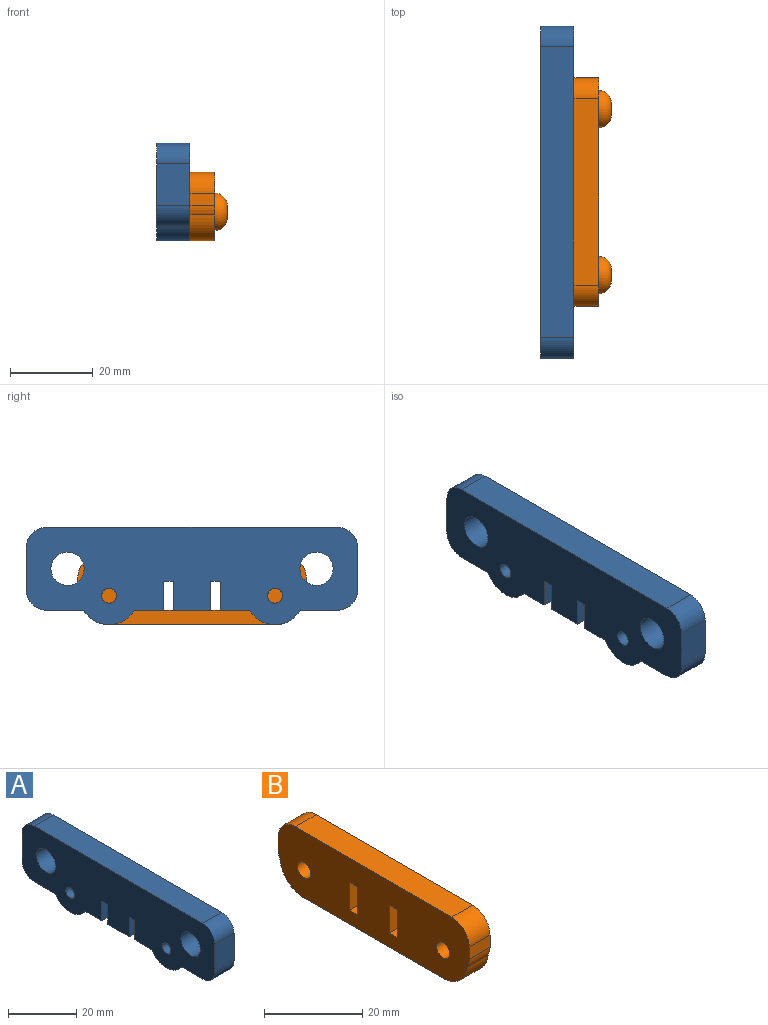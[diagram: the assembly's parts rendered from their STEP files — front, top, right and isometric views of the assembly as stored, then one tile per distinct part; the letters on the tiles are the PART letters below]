
ASSEMBLY  parts=2 mates=1
PART A: 40 faces, bbox 8x80x23.5 mm
  f0: cylinder r=1.8mm len=5mm, axis (-1,0,0), area 56.5mm2, adj f25,f39
  f1: cylinder r=1.8mm len=5mm, axis (-1,0,0), area 56.5mm2, adj f25,f32
  f2: plane 80x23.5mm, normal (1,0,0), area 1450.3mm2, adj f3,f4,f5,f6,f7,f8,f9,f10
  f3: plane 8x2.4mm, normal (0,0,-1), area 19.2mm2, adj f2,f4,f24,f25
  f4: plane 8x7mm, normal (0,-1,0), area 56mm2, adj f2,f3,f5,f25
  f5: plane 8x7.04mm, normal (0,0,-1), area 56.3mm2, adj f2,f4,f6,f25
  f6: cylinder r=7mm len=12.12mm, axis (-1,0,0), area 117.3mm2, adj f2,f5,f7,f25
  f7: plane 8.94x8mm, normal (0,0,-1), area 71.5mm2, adj f2,f6,f8,f25
  f8: cylinder r=5mm len=8mm, axis (-1,0,0), area 62.8mm2, adj f2,f7,f9,f25
  f9: plane 10x8mm, normal (0,1,0), area 80mm2, adj f2,f8,f10,f25
  f10: cylinder r=5mm len=8mm, axis (-1,0,0), area 62.8mm2, adj f2,f9,f11,f25
  f11: plane 70x8mm, normal (0,0,1), area 560mm2, adj f2,f10,f12,f25
  f12: cylinder r=5mm len=8mm, axis (-1,0,0), area 62.8mm2, adj f2,f11,f13,f25
  f13: plane 10x8mm, normal (0,-1,0), area 80mm2, adj f2,f12,f14,f25
  f14: cylinder r=5mm len=8mm, axis (-1,0,0), area 62.8mm2, adj f2,f13,f15,f25
  f15: plane 8.94x8mm, normal (0,0,-1), area 71.5mm2, adj f2,f14,f16,f25
  f16: cylinder r=7mm len=12.12mm, axis (-1,0,0), area 117.3mm2, adj f2,f15,f17,f25
  f17: plane 8x7.04mm, normal (0,0,-1), area 56.3mm2, adj f2,f16,f18,f25
  f18: plane 8x7mm, normal (0,1,0), area 56mm2, adj f2,f17,f19,f25
  f19: plane 8x2.4mm, normal (0,0,-1), area 19.2mm2, adj f2,f18,f20,f25
  f20: plane 8x7mm, normal (0,-1,0), area 56mm2, adj f2,f19,f21,f25
  f21: plane 9x8mm, normal (0,0,-1), area 72mm2, adj f2,f20,f24,f25
  f22: cylinder r=4mm len=8mm, axis (-1,0,0), area 201.1mm2, adj f2,f25
  f23: cylinder r=4mm len=8mm, axis (-1,0,0), area 201.1mm2, adj f2,f25
  f24: plane 8x7mm, normal (0,1,0), area 56mm2, adj f2,f3,f21,f25
  f25: plane 80x23.5mm, normal (-1,0,0), area 1484.2mm2, adj f0,f1,f3,f4,f5,f6,f7,f8
  f26: plane 3x2.8mm, normal (0,0.87,-0.5), area 9.7mm2, adj f2,f27,f31,f32
  f27: plane 3x2.8mm, normal (0,0.87,0.5), area 9.7mm2, adj f2,f26,f28,f32
  f28: plane 3.23x3mm, normal (0,0,1), area 9.7mm2, adj f2,f27,f29,f32
  f29: plane 3x2.8mm, normal (0,-0.87,0.5), area 9.7mm2, adj f2,f28,f30,f32
  f30: plane 3x2.8mm, normal (0,-0.87,-0.5), area 9.7mm2, adj f2,f29,f31,f32
  f31: plane 3.23x3mm, normal (0,0,-1), area 9.7mm2, adj f2,f26,f30,f32
  f32: plane 6.47x5.6mm, normal (1,0,0), area 17mm2, adj f1,f26,f27,f28,f29,f30,f31
  f33: plane 3x2.8mm, normal (0,0.87,-0.5), area 9.7mm2, adj f2,f34,f38,f39
  f34: plane 3x2.8mm, normal (0,0.87,0.5), area 9.7mm2, adj f2,f33,f35,f39
  f35: plane 3.23x3mm, normal (0,0,1), area 9.7mm2, adj f2,f34,f36,f39
  f36: plane 3x2.8mm, normal (0,-0.87,0.5), area 9.7mm2, adj f2,f35,f37,f39
  f37: plane 3x2.8mm, normal (0,-0.87,-0.5), area 9.7mm2, adj f2,f36,f38,f39
  f38: plane 3.23x3mm, normal (0,0,-1), area 9.7mm2, adj f2,f33,f37,f39
  f39: plane 6.47x5.6mm, normal (1,0,0), area 17mm2, adj f0,f33,f34,f35,f36,f37,f38
PART B: 28 faces, bbox 9x55x16.5 mm
  f0: plane 6x2.4mm, normal (0,0,1), area 14.4mm2, adj f1,f16,f20,f21
  f1: plane 7x6mm, normal (0,1,0), area 42mm2, adj f0,f2,f20,f21
  f2: plane 6x2.4mm, normal (0,0,-1), area 14.4mm2, adj f1,f16,f20,f21
  f3: plane 6x2.4mm, normal (0,0,1), area 14.4mm2, adj f4,f17,f20,f21
  f4: plane 7x6mm, normal (0,1,0), area 42mm2, adj f3,f5,f20,f21
  f5: plane 6x2.4mm, normal (0,0,-1), area 14.4mm2, adj f4,f17,f20,f21
  f6: cylinder r=7mm len=6.87mm, axis (-1,0,0), area 60.9mm2, adj f7,f18,f20,f21
  f7: plane 40.09x6mm, normal (0,0,-1), area 240.5mm2, adj f6,f8,f20,f21
  f8: cylinder r=7mm len=6.96mm, axis (-1,0,0), area 61.4mm2, adj f7,f9,f20,f21
  f9: cylinder r=5mm len=6mm, axis (-1,0,0), area 14.1mm2, adj f8,f10,f20,f21
  f10: plane 6x3mm, normal (0,1,0), area 18mm2, adj f9,f11,f20,f21
  f11: cylinder r=5mm len=6mm, axis (-1,0,0), area 47.1mm2, adj f10,f12,f20,f21
  f12: plane 45x6mm, normal (0,0,1), area 270mm2, adj f11,f13,f20,f21
  f13: cylinder r=5mm len=6mm, axis (-1,0,0), area 47.1mm2, adj f12,f14,f20,f21
  f14: plane 6x3mm, normal (0,-1,0), area 18mm2, adj f13,f18,f20,f21
  f15: cylinder r=1.9mm len=6mm, axis (-1,0,0), area 71.6mm2, adj f21,f25
  f16: plane 7x6mm, normal (0,-1,0), area 42mm2, adj f0,f2,f20,f21
  f17: plane 7x6mm, normal (0,-1,0), area 42mm2, adj f3,f5,f20,f21
  f18: cylinder r=5mm len=6mm, axis (-1,0,0), area 14.1mm2, adj f6,f14,f20,f21
  f19: cylinder r=1.9mm len=6mm, axis (-1,0,0), area 71.6mm2, adj f21,f23
  f20: plane 55x16.5mm, normal (1,0,0), area 707.9mm2, adj f0,f1,f2,f3,f4,f5,f6,f7
  f21: plane 55x16.5mm, normal (-1,0,0), area 812.4mm2, adj f0,f1,f2,f3,f4,f5,f6,f7
  f22: plane 3x3mm, normal (1,0,0), area 7.1mm2, adj f26
  f23: plane 3.8x3.8mm, normal (-1,0,0), area 11.3mm2, adj f19
  f24: plane 3x3mm, normal (1,0,0), area 7.1mm2, adj f27
  f25: plane 3.8x3.8mm, normal (-1,0,0), area 11.3mm2, adj f15
  f26: torus R=1.5mm, axis (1,0,0), area 101mm2, adj f20,f22
  f27: torus R=1.5mm, axis (1,0,0), area 101mm2, adj f20,f24
PLACE A t=(-34.78,15.1,-17.42)mm
PLACE B t=(-30.78,15.1,49.27)mm
MATE fastened B.f21 <-> A.f2  axis (-1,0,0) through (-30.78,8.2,42.77)mm
